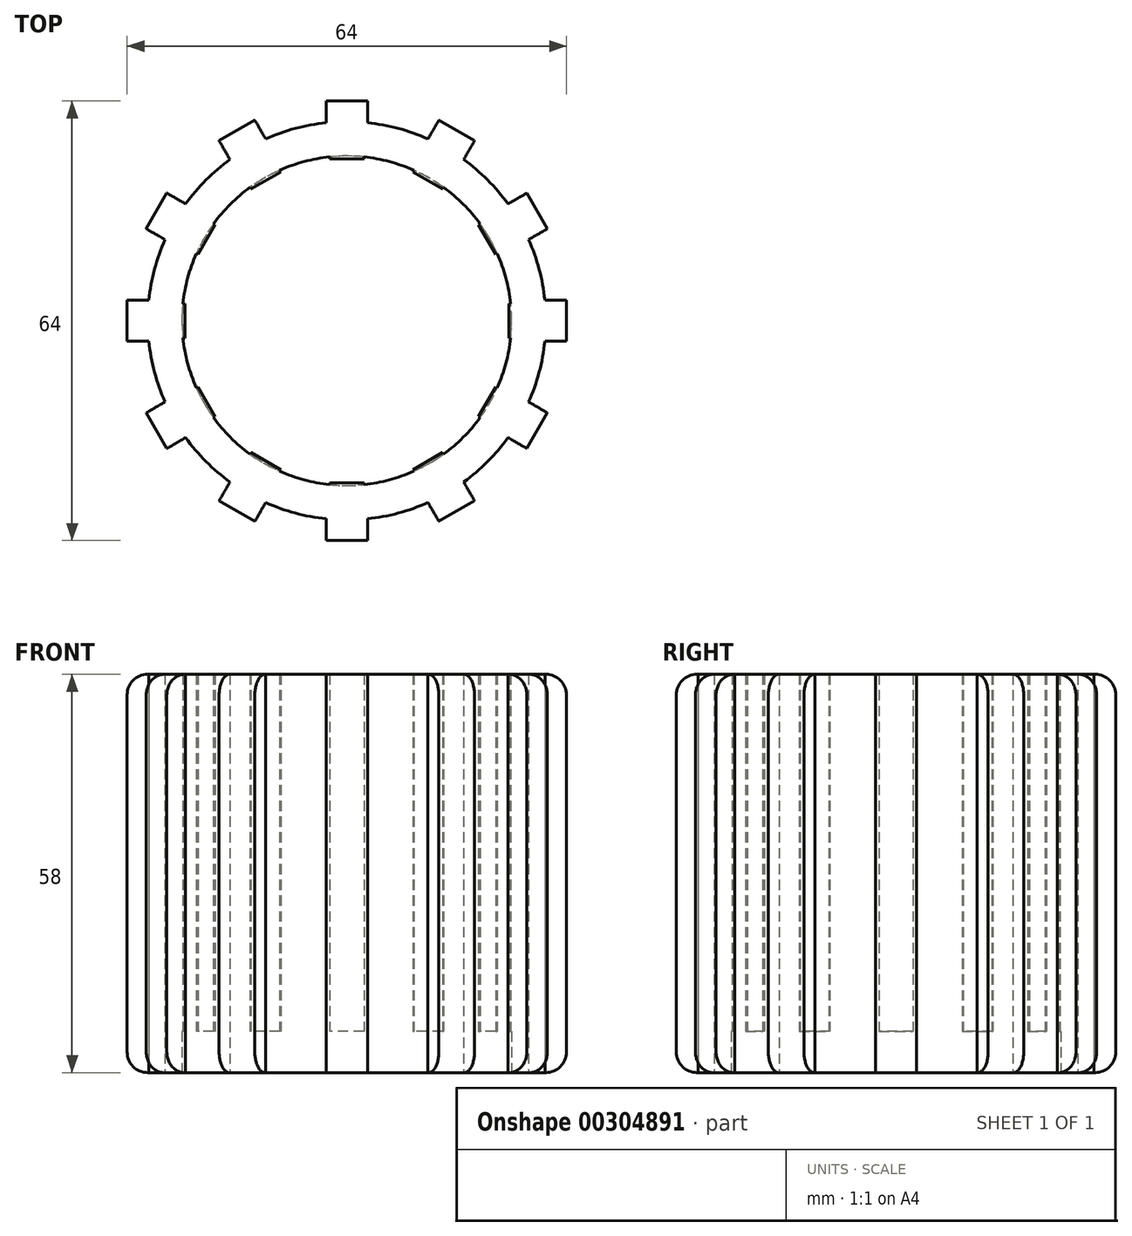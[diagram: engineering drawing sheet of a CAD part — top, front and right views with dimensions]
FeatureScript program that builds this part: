
annotation { "Feature Type Name" : "Feature", "Feature Type Description" : "" }
export const myFeature = defineFeature(function(context is Context, id is Id, definition is map)
    precondition{}
    {
        {
            var Q0;
            Q0=qCreatedBy(makeId("Top.planeOp"),FACE);
            var sketch = newSketch(context, id + "F0", { "sketchPlane" : qUnion([Q0])});
            skCircle(sketch, "E0", {"center": v(0, 0) * mm, "radius": 24 * mm});
            skCircle(sketch, "E1", {"center": v(0, 0) * mm, "radius": 29 * mm});
            skLineSegment(sketch, "E2.bottom", {"start": v(-3, 32) * mm, "end": v(3, 32) * mm});
            skLineSegment(sketch, "E2.top", {"start": v(-3, 26) * mm, "end": v(3, 26) * mm});
            skLineSegment(sketch, "E2.left", {"start": v(-3, 32) * mm, "end": v(-3, 26) * mm});
            skLineSegment(sketch, "E2.right", {"start": v(3, 32) * mm, "end": v(3, 26) * mm});
            skPoint(sketch, "E2.middle", {"position": v(0, 29) * mm});
            skLineSegment(sketch, "E3.1.0", {"start": v(-18.6, 26.21) * mm, "end": v(-15.6, 21.02) * mm});
            skLineSegment(sketch, "E3.1.1", {"start": v(-18.6, 26.21) * mm, "end": v(-13.4, 29.21) * mm});
            skLineSegment(sketch, "E3.1.2", {"start": v(-13.4, 29.21) * mm, "end": v(-10.4, 24.02) * mm});
            skLineSegment(sketch, "E3.2.0", {"start": v(-29.21, 13.4) * mm, "end": v(-24.02, 10.4) * mm});
            skLineSegment(sketch, "E3.2.1", {"start": v(-29.21, 13.4) * mm, "end": v(-26.21, 18.6) * mm});
            skLineSegment(sketch, "E3.2.2", {"start": v(-26.21, 18.6) * mm, "end": v(-21.02, 15.6) * mm});
            skLineSegment(sketch, "E4.2.3.0", {"start": v(-32, -3) * mm, "end": v(-26, -3) * mm});
            skLineSegment(sketch, "E4.3.3.0", {"start": v(-32, -3) * mm, "end": v(-32, 3) * mm});
            skLineSegment(sketch, "E4.6.3.0", {"start": v(-32, 3) * mm, "end": v(-26, 3) * mm});
            skLineSegment(sketch, "E4.2.4.0", {"start": v(-26.21, -18.6) * mm, "end": v(-21.02, -15.6) * mm});
            skLineSegment(sketch, "E4.3.4.0", {"start": v(-26.21, -18.6) * mm, "end": v(-29.21, -13.4) * mm});
            skLineSegment(sketch, "E4.6.4.0", {"start": v(-29.21, -13.4) * mm, "end": v(-24.02, -10.4) * mm});
            skLineSegment(sketch, "E4.2.5.0", {"start": v(-13.4, -29.21) * mm, "end": v(-10.4, -24.02) * mm});
            skLineSegment(sketch, "E4.3.5.0", {"start": v(-13.4, -29.21) * mm, "end": v(-18.6, -26.21) * mm});
            skLineSegment(sketch, "E4.6.5.0", {"start": v(-18.6, -26.21) * mm, "end": v(-15.6, -21.02) * mm});
            skLineSegment(sketch, "E4.2.6.0", {"start": v(3, -32) * mm, "end": v(3, -26) * mm});
            skLineSegment(sketch, "E4.3.6.0", {"start": v(3, -32) * mm, "end": v(-3, -32) * mm});
            skLineSegment(sketch, "E4.6.6.0", {"start": v(-3, -32) * mm, "end": v(-3, -26) * mm});
            skLineSegment(sketch, "E4.2.7.0", {"start": v(18.6, -26.21) * mm, "end": v(15.6, -21.02) * mm});
            skLineSegment(sketch, "E4.3.7.0", {"start": v(18.6, -26.21) * mm, "end": v(13.4, -29.21) * mm});
            skLineSegment(sketch, "E4.6.7.0", {"start": v(13.4, -29.21) * mm, "end": v(10.4, -24.02) * mm});
            skLineSegment(sketch, "E4.2.8.0", {"start": v(29.21, -13.4) * mm, "end": v(24.02, -10.4) * mm});
            skLineSegment(sketch, "E4.3.8.0", {"start": v(29.21, -13.4) * mm, "end": v(26.21, -18.6) * mm});
            skLineSegment(sketch, "E4.6.8.0", {"start": v(26.21, -18.6) * mm, "end": v(21.02, -15.6) * mm});
            skLineSegment(sketch, "E4.2.9.0", {"start": v(32, 3) * mm, "end": v(26, 3) * mm});
            skLineSegment(sketch, "E4.3.9.0", {"start": v(32, 3) * mm, "end": v(32, -3) * mm});
            skLineSegment(sketch, "E4.6.9.0", {"start": v(32, -3) * mm, "end": v(26, -3) * mm});
            skLineSegment(sketch, "E4.2.10.0", {"start": v(26.21, 18.6) * mm, "end": v(21.02, 15.6) * mm});
            skLineSegment(sketch, "E4.3.10.0", {"start": v(26.21, 18.6) * mm, "end": v(29.21, 13.4) * mm});
            skLineSegment(sketch, "E4.6.10.0", {"start": v(29.21, 13.4) * mm, "end": v(24.02, 10.4) * mm});
            skLineSegment(sketch, "E4.2.11.0", {"start": v(13.4, 29.21) * mm, "end": v(10.4, 24.02) * mm});
            skLineSegment(sketch, "E4.3.11.0", {"start": v(13.4, 29.21) * mm, "end": v(18.6, 26.21) * mm});
            skLineSegment(sketch, "E4.6.11.0", {"start": v(18.6, 26.21) * mm, "end": v(15.6, 21.02) * mm});
            skLineSegment(sketch, "E5.bottom", {"start": v(2.5, -23.6) * mm, "end": v(-2.5, -23.6) * mm});
            skLineSegment(sketch, "E5.left", {"start": v(2.5, -23.6) * mm, "end": v(2.5, -24.4) * mm});
            skLineSegment(sketch, "E5.right", {"start": v(-2.5, -23.6) * mm, "end": v(-2.5, -24.4) * mm});
            skPoint(sketch, "E5.middle", {"position": v(0, -24) * mm});
            skLineSegment(sketch, "E6.1.0", {"start": v(13.97, -19.19) * mm, "end": v(9.63, -21.69) * mm});
            skLineSegment(sketch, "E6.1.1", {"start": v(9.63, -21.69) * mm, "end": v(10.03, -22.38) * mm});
            skLineSegment(sketch, "E6.1.2", {"start": v(13.97, -19.19) * mm, "end": v(14.37, -19.88) * mm});
            skLineSegment(sketch, "E6.2.0", {"start": v(21.69, -9.63) * mm, "end": v(19.19, -13.97) * mm});
            skLineSegment(sketch, "E6.2.1", {"start": v(19.19, -13.97) * mm, "end": v(19.88, -14.37) * mm});
            skLineSegment(sketch, "E6.2.2", {"start": v(21.69, -9.63) * mm, "end": v(22.38, -10.03) * mm});
            skLineSegment(sketch, "E6.3.0", {"start": v(23.6, 2.5) * mm, "end": v(23.6, -2.5) * mm});
            skLineSegment(sketch, "E6.3.1", {"start": v(23.6, -2.5) * mm, "end": v(24.4, -2.5) * mm});
            skLineSegment(sketch, "E6.3.2", {"start": v(23.6, 2.5) * mm, "end": v(24.4, 2.5) * mm});
            skLineSegment(sketch, "E6.4.0", {"start": v(19.19, 13.97) * mm, "end": v(21.69, 9.63) * mm});
            skLineSegment(sketch, "E6.4.1", {"start": v(21.69, 9.63) * mm, "end": v(22.38, 10.03) * mm});
            skLineSegment(sketch, "E6.4.2", {"start": v(19.19, 13.97) * mm, "end": v(19.88, 14.37) * mm});
            skLineSegment(sketch, "E6.5.0", {"start": v(9.63, 21.69) * mm, "end": v(13.97, 19.19) * mm});
            skLineSegment(sketch, "E6.5.1", {"start": v(13.97, 19.19) * mm, "end": v(14.37, 19.88) * mm});
            skLineSegment(sketch, "E6.5.2", {"start": v(9.63, 21.69) * mm, "end": v(10.03, 22.38) * mm});
            skLineSegment(sketch, "E6.6.0", {"start": v(-2.5, 23.6) * mm, "end": v(2.5, 23.6) * mm});
            skLineSegment(sketch, "E6.6.1", {"start": v(2.5, 23.6) * mm, "end": v(2.5, 24.4) * mm});
            skLineSegment(sketch, "E6.6.2", {"start": v(-2.5, 23.6) * mm, "end": v(-2.5, 24.4) * mm});
            skLineSegment(sketch, "E6.7.0", {"start": v(-13.97, 19.19) * mm, "end": v(-9.63, 21.69) * mm});
            skLineSegment(sketch, "E6.7.1", {"start": v(-9.63, 21.69) * mm, "end": v(-10.03, 22.38) * mm});
            skLineSegment(sketch, "E6.7.2", {"start": v(-13.97, 19.19) * mm, "end": v(-14.37, 19.88) * mm});
            skLineSegment(sketch, "E6.8.0", {"start": v(-21.69, 9.63) * mm, "end": v(-19.19, 13.97) * mm});
            skLineSegment(sketch, "E6.8.1", {"start": v(-19.19, 13.97) * mm, "end": v(-19.88, 14.37) * mm});
            skLineSegment(sketch, "E6.8.2", {"start": v(-21.69, 9.63) * mm, "end": v(-22.38, 10.03) * mm});
            skLineSegment(sketch, "E6.9.0", {"start": v(-23.6, -2.5) * mm, "end": v(-23.6, 2.5) * mm});
            skLineSegment(sketch, "E6.9.1", {"start": v(-23.6, 2.5) * mm, "end": v(-24.4, 2.5) * mm});
            skLineSegment(sketch, "E6.9.2", {"start": v(-23.6, -2.5) * mm, "end": v(-24.4, -2.5) * mm});
            skLineSegment(sketch, "E6.10.0", {"start": v(-19.19, -13.97) * mm, "end": v(-21.69, -9.63) * mm});
            skLineSegment(sketch, "E6.10.1", {"start": v(-21.69, -9.63) * mm, "end": v(-22.38, -10.03) * mm});
            skLineSegment(sketch, "E6.10.2", {"start": v(-19.19, -13.97) * mm, "end": v(-19.88, -14.37) * mm});
            skLineSegment(sketch, "E6.11.0", {"start": v(-9.63, -21.69) * mm, "end": v(-13.97, -19.19) * mm});
            skLineSegment(sketch, "E6.11.1", {"start": v(-13.97, -19.19) * mm, "end": v(-14.37, -19.88) * mm});
            skLineSegment(sketch, "E6.11.2", {"start": v(-9.63, -21.69) * mm, "end": v(-10.03, -22.38) * mm});
            skSolve(sketch);
        }
        {
            var Q0;
            Q0=makeQuery(id+"F0.imprint","IMPRINT",FACE,{"disambiguationData":[TD([[makeQuery(id+"F0.imprint","IMPRINT",EDGE,{"derivedFrom":sQuery(id+"F0.wireOp",EDGE,"E0")}),-1.0]])]});
            var Q1;
            {var subQ5=sQuery(id+"F0.wireOp",EDGE,"E4.3.6.0");Q1=makeQuery(id+"F0.imprint","IMPRINT",FACE,{"disambiguationData":[TD([[makeQuery(id+"F0.imprint","IMPRINT",EDGE,{"derivedFrom":subQ5}),-1.0]])]});}
            var Q2;
            {var subQ5=sQuery(id+"F0.wireOp",EDGE,"E4.3.5.0");Q2=makeQuery(id+"F0.imprint","IMPRINT",FACE,{"disambiguationData":[TD([[makeQuery(id+"F0.imprint","IMPRINT",EDGE,{"derivedFrom":subQ5}),-1.0]])]});}
            var Q3;
            {var subQ5=sQuery(id+"F0.wireOp",EDGE,"E4.3.4.0");Q3=makeQuery(id+"F0.imprint","IMPRINT",FACE,{"disambiguationData":[TD([[makeQuery(id+"F0.imprint","IMPRINT",EDGE,{"derivedFrom":subQ5}),-1.0]])]});}
            var Q4;
            {var subQ5=sQuery(id+"F0.wireOp",EDGE,"E4.3.3.0");Q4=makeQuery(id+"F0.imprint","IMPRINT",FACE,{"disambiguationData":[TD([[makeQuery(id+"F0.imprint","IMPRINT",EDGE,{"derivedFrom":subQ5}),-1.0]])]});}
            var Q5;
            {var subQ5=sQuery(id+"F0.wireOp",EDGE,"E3.2.1");Q5=makeQuery(id+"F0.imprint","IMPRINT",FACE,{"disambiguationData":[TD([[makeQuery(id+"F0.imprint","IMPRINT",EDGE,{"derivedFrom":subQ5}),-1.0]])]});}
            var Q6;
            {var subQ5=sQuery(id+"F0.wireOp",EDGE,"E3.1.1");Q6=makeQuery(id+"F0.imprint","IMPRINT",FACE,{"disambiguationData":[TD([[makeQuery(id+"F0.imprint","IMPRINT",EDGE,{"derivedFrom":subQ5}),-1.0]])]});}
            var Q7;
            {var subQ5=sQuery(id+"F0.wireOp",EDGE,"E2.bottom");Q7=makeQuery(id+"F0.imprint","IMPRINT",FACE,{"disambiguationData":[TD([[makeQuery(id+"F0.imprint","IMPRINT",EDGE,{"derivedFrom":subQ5}),-1.0]])]});}
            var Q8;
            {var subQ5=sQuery(id+"F0.wireOp",EDGE,"E4.3.11.0");Q8=makeQuery(id+"F0.imprint","IMPRINT",FACE,{"disambiguationData":[TD([[makeQuery(id+"F0.imprint","IMPRINT",EDGE,{"derivedFrom":subQ5}),-1.0]])]});}
            var Q9;
            {var subQ5=sQuery(id+"F0.wireOp",EDGE,"E2.top");Q9=makeQuery(id+"F0.imprint","IMPRINT",FACE,{"disambiguationData":[TD([[makeQuery(id+"F0.imprint","IMPRINT",EDGE,{"derivedFrom":subQ5}),1.0]])]});}
            var Q10;
            {var subQ5=sQuery(id+"F0.wireOp",EDGE,"E4.3.10.0");Q10=makeQuery(id+"F0.imprint","IMPRINT",FACE,{"disambiguationData":[TD([[makeQuery(id+"F0.imprint","IMPRINT",EDGE,{"derivedFrom":subQ5}),-1.0]])]});}
            var Q11;
            {var subQ5=sQuery(id+"F0.wireOp",EDGE,"E4.3.9.0");Q11=makeQuery(id+"F0.imprint","IMPRINT",FACE,{"disambiguationData":[TD([[makeQuery(id+"F0.imprint","IMPRINT",EDGE,{"derivedFrom":subQ5}),-1.0]])]});}
            var Q12;
            {var subQ5=sQuery(id+"F0.wireOp",EDGE,"E4.3.8.0");Q12=makeQuery(id+"F0.imprint","IMPRINT",FACE,{"disambiguationData":[TD([[makeQuery(id+"F0.imprint","IMPRINT",EDGE,{"derivedFrom":subQ5}),-1.0]])]});}
            var Q13;
            {var subQ5=sQuery(id+"F0.wireOp",EDGE,"E4.3.7.0");Q13=makeQuery(id+"F0.imprint","IMPRINT",FACE,{"disambiguationData":[TD([[makeQuery(id+"F0.imprint","IMPRINT",EDGE,{"derivedFrom":subQ5}),-1.0]])]});}
            var Q14;
            {var subQ5=sQuery(id+"F0.wireOp",EDGE,"E6.2.0");Q14=makeQuery(id+"F0.imprint","IMPRINT",FACE,{"disambiguationData":[TD([[makeQuery(id+"F0.imprint","IMPRINT",EDGE,{"derivedFrom":subQ5}),1.0]])]});}
            var Q15;
            {var subQ5=sQuery(id+"F0.wireOp",EDGE,"E6.1.0");Q15=makeQuery(id+"F0.imprint","IMPRINT",FACE,{"disambiguationData":[TD([[makeQuery(id+"F0.imprint","IMPRINT",EDGE,{"derivedFrom":subQ5}),1.0]])]});}
            var Q16;
            {var subQ5=sQuery(id+"F0.wireOp",EDGE,"E5.bottom");Q16=makeQuery(id+"F0.imprint","IMPRINT",FACE,{"disambiguationData":[TD([[makeQuery(id+"F0.imprint","IMPRINT",EDGE,{"derivedFrom":subQ5}),1.0]])]});}
            var Q17;
            {var subQ5=sQuery(id+"F0.wireOp",EDGE,"E6.11.0");Q17=makeQuery(id+"F0.imprint","IMPRINT",FACE,{"disambiguationData":[TD([[makeQuery(id+"F0.imprint","IMPRINT",EDGE,{"derivedFrom":subQ5}),1.0]])]});}
            var Q18;
            {var subQ5=sQuery(id+"F0.wireOp",EDGE,"E6.10.0");Q18=makeQuery(id+"F0.imprint","IMPRINT",FACE,{"disambiguationData":[TD([[makeQuery(id+"F0.imprint","IMPRINT",EDGE,{"derivedFrom":subQ5}),1.0]])]});}
            var Q19;
            {var subQ5=sQuery(id+"F0.wireOp",EDGE,"E6.9.0");Q19=makeQuery(id+"F0.imprint","IMPRINT",FACE,{"disambiguationData":[TD([[makeQuery(id+"F0.imprint","IMPRINT",EDGE,{"derivedFrom":subQ5}),1.0]])]});}
            var Q20;
            {var subQ5=sQuery(id+"F0.wireOp",EDGE,"E6.8.0");Q20=makeQuery(id+"F0.imprint","IMPRINT",FACE,{"disambiguationData":[TD([[makeQuery(id+"F0.imprint","IMPRINT",EDGE,{"derivedFrom":subQ5}),1.0]])]});}
            var Q21;
            {var subQ5=sQuery(id+"F0.wireOp",EDGE,"E6.7.0");Q21=makeQuery(id+"F0.imprint","IMPRINT",FACE,{"disambiguationData":[TD([[makeQuery(id+"F0.imprint","IMPRINT",EDGE,{"derivedFrom":subQ5}),1.0]])]});}
            var Q22;
            {var subQ5=sQuery(id+"F0.wireOp",EDGE,"E6.6.0");Q22=makeQuery(id+"F0.imprint","IMPRINT",FACE,{"disambiguationData":[TD([[makeQuery(id+"F0.imprint","IMPRINT",EDGE,{"derivedFrom":subQ5}),1.0]])]});}
            var Q23;
            {var subQ5=sQuery(id+"F0.wireOp",EDGE,"E6.5.0");Q23=makeQuery(id+"F0.imprint","IMPRINT",FACE,{"disambiguationData":[TD([[makeQuery(id+"F0.imprint","IMPRINT",EDGE,{"derivedFrom":subQ5}),1.0]])]});}
            var Q24;
            {var subQ5=sQuery(id+"F0.wireOp",EDGE,"E6.4.0");Q24=makeQuery(id+"F0.imprint","IMPRINT",FACE,{"disambiguationData":[TD([[makeQuery(id+"F0.imprint","IMPRINT",EDGE,{"derivedFrom":subQ5}),1.0]])]});}
            var Q25;
            {var subQ5=sQuery(id+"F0.wireOp",EDGE,"E6.3.0");Q25=makeQuery(id+"F0.imprint","IMPRINT",FACE,{"disambiguationData":[TD([[makeQuery(id+"F0.imprint","IMPRINT",EDGE,{"derivedFrom":subQ5}),1.0]])]});}
            extrude(context, id + "F1", {"entities" : qUnion([Q0, Q1, Q2, Q3, Q4, Q5, Q6, Q7, Q8, Q9, Q10, Q11, Q12, Q13, Q14, Q15, Q16, Q17, Q18, Q19, Q20, Q21, Q22, Q23, Q24, Q25]), "depth" : 58 * mm});
        }
        {
            var Q0;
            Q0=makeQuery(id+"F1.opExtrude","CAP_EDGE",EDGE,{"disambiguationData":[OSD([sQuery(id+"F0.wireOp",EDGE,"E4.3.9.0")])],"isStart":true});
            var Q1;
            Q1=makeQuery(id+"F1.opExtrude","CAP_EDGE",EDGE,{"disambiguationData":[OSD([sQuery(id+"F0.wireOp",EDGE,"E4.3.10.0")])],"isStart":true});
            var Q2;
            Q2=makeQuery(id+"F1.opExtrude","CAP_EDGE",EDGE,{"disambiguationData":[OSD([sQuery(id+"F0.wireOp",EDGE,"E4.3.11.0")])],"isStart":true});
            var Q3;
            Q3=makeQuery(id+"F1.opExtrude","CAP_EDGE",EDGE,{"disambiguationData":[OSD([sQuery(id+"F0.wireOp",EDGE,"E2.bottom")])],"isStart":true});
            var Q4;
            Q4=makeQuery(id+"F1.opExtrude","CAP_EDGE",EDGE,{"disambiguationData":[OSD([sQuery(id+"F0.wireOp",EDGE,"E3.1.1")])],"isStart":true});
            var Q5;
            Q5=makeQuery(id+"F1.opExtrude","CAP_EDGE",EDGE,{"disambiguationData":[OSD([sQuery(id+"F0.wireOp",EDGE,"E3.2.1")])],"isStart":true});
            var Q6;
            Q6=makeQuery(id+"F1.opExtrude","CAP_EDGE",EDGE,{"disambiguationData":[OSD([sQuery(id+"F0.wireOp",EDGE,"E4.3.3.0")])],"isStart":true});
            var Q7;
            Q7=makeQuery(id+"F1.opExtrude","CAP_EDGE",EDGE,{"disambiguationData":[OSD([sQuery(id+"F0.wireOp",EDGE,"E4.3.4.0")])],"isStart":true});
            var Q8;
            Q8=makeQuery(id+"F1.opExtrude","CAP_EDGE",EDGE,{"disambiguationData":[OSD([sQuery(id+"F0.wireOp",EDGE,"E4.3.5.0")])],"isStart":true});
            var Q9;
            Q9=makeQuery(id+"F1.opExtrude","CAP_EDGE",EDGE,{"disambiguationData":[OSD([sQuery(id+"F0.wireOp",EDGE,"E4.3.6.0")])],"isStart":true});
            var Q10;
            Q10=makeQuery(id+"F1.opExtrude","CAP_EDGE",EDGE,{"disambiguationData":[OSD([sQuery(id+"F0.wireOp",EDGE,"E4.3.7.0")])],"isStart":true});
            var Q11;
            Q11=makeQuery(id+"F1.opExtrude","CAP_EDGE",EDGE,{"disambiguationData":[OSD([sQuery(id+"F0.wireOp",EDGE,"E4.3.8.0")])],"isStart":true});
            var Q12;
            Q12=makeQuery(id+"F1.opExtrude","CAP_EDGE",EDGE,{"disambiguationData":[OSD([sQuery(id+"F0.wireOp",EDGE,"E4.3.5.0")])],"isStart":false});
            var Q13;
            Q13=makeQuery(id+"F1.opExtrude","CAP_EDGE",EDGE,{"disambiguationData":[OSD([sQuery(id+"F0.wireOp",EDGE,"E4.3.6.0")])],"isStart":false});
            var Q14;
            Q14=makeQuery(id+"F1.opExtrude","CAP_EDGE",EDGE,{"disambiguationData":[OSD([sQuery(id+"F0.wireOp",EDGE,"E4.3.7.0")])],"isStart":false});
            var Q15;
            Q15=makeQuery(id+"F1.opExtrude","CAP_EDGE",EDGE,{"disambiguationData":[OSD([sQuery(id+"F0.wireOp",EDGE,"E4.3.8.0")])],"isStart":false});
            var Q16;
            Q16=makeQuery(id+"F1.opExtrude","CAP_EDGE",EDGE,{"disambiguationData":[OSD([sQuery(id+"F0.wireOp",EDGE,"E4.3.9.0")])],"isStart":false});
            var Q17;
            Q17=makeQuery(id+"F1.opExtrude","CAP_EDGE",EDGE,{"disambiguationData":[OSD([sQuery(id+"F0.wireOp",EDGE,"E4.3.10.0")])],"isStart":false});
            var Q18;
            Q18=makeQuery(id+"F1.opExtrude","CAP_EDGE",EDGE,{"disambiguationData":[OSD([sQuery(id+"F0.wireOp",EDGE,"E4.3.11.0")])],"isStart":false});
            var Q19;
            Q19=makeQuery(id+"F1.opExtrude","CAP_EDGE",EDGE,{"disambiguationData":[OSD([sQuery(id+"F0.wireOp",EDGE,"E2.bottom")])],"isStart":false});
            var Q20;
            Q20=makeQuery(id+"F1.opExtrude","CAP_EDGE",EDGE,{"disambiguationData":[OSD([sQuery(id+"F0.wireOp",EDGE,"E3.1.1")])],"isStart":false});
            var Q21;
            Q21=makeQuery(id+"F1.opExtrude","CAP_EDGE",EDGE,{"disambiguationData":[OSD([sQuery(id+"F0.wireOp",EDGE,"E3.2.1")])],"isStart":false});
            var Q22;
            Q22=makeQuery(id+"F1.opExtrude","CAP_EDGE",EDGE,{"disambiguationData":[OSD([sQuery(id+"F0.wireOp",EDGE,"E4.3.3.0")])],"isStart":false});
            var Q23;
            Q23=makeQuery(id+"F1.opExtrude","CAP_EDGE",EDGE,{"disambiguationData":[OSD([sQuery(id+"F0.wireOp",EDGE,"E4.3.4.0")])],"isStart":false});
            fillet(context, id + "F2", {"entities" : qUnion([Q0, Q1, Q2, Q3, Q4, Q5, Q6, Q7, Q8, Q9, Q10, Q11, Q12, Q13, Q14, Q15, Q16, Q17, Q18, Q19, Q20, Q21, Q22, Q23]), "radius" : 3 * mm, "tangentPropagation" : true, "allowEdgeOverflow" : false});
        }
        {
            var Q0;
            {var subQ58=sQuery(id+"F0.wireOp",EDGE,"E5.bottom");Q0=makeQuery(id+"F0.imprint","IMPRINT",FACE,{"disambiguationData":[TD([[makeQuery(id+"F0.imprint","IMPRINT",EDGE,{"derivedFrom":subQ58}),-1.0]])]});}
            var sketch = newSketch(context, id + "F3", { "sketchPlane" : qUnion([Q0])});
            skCircle(sketch, "E7", {"center": v(0, 0) * mm, "radius": 24 * mm});
            skSolve(sketch);
        }
        {
            var Q0;
            {var subQ58=sQuery(id+"F0.wireOp",EDGE,"E5.bottom");Q0=makeQuery(id+"F0.imprint","IMPRINT",FACE,{"disambiguationData":[TD([[makeQuery(id+"F0.imprint","IMPRINT",EDGE,{"derivedFrom":subQ58}),-1.0]])]});}
            var Q1;
            Q1 = qSketchRegion(id + "F3", true);
            extrude(context, id + "F4", {"entities" : qUnion([Q0, Q1]), "operationType" : NewBodyOperationType.REMOVE, "depth" : 6 * mm});
        }
    });
